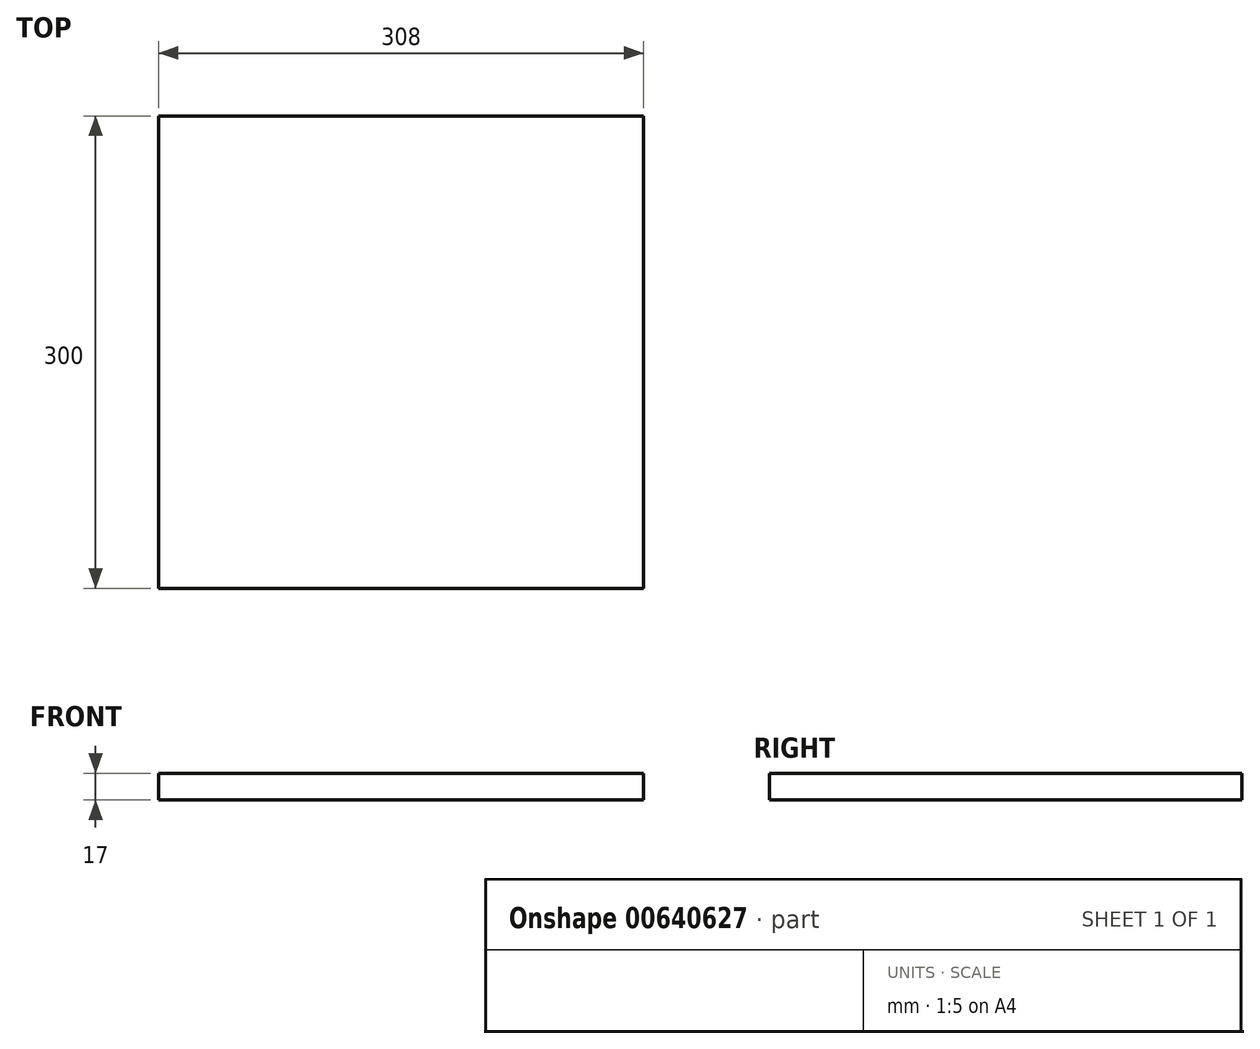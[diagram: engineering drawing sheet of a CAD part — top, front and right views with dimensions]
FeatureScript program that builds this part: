
annotation { "Feature Type Name" : "Feature", "Feature Type Description" : "" }
export const myFeature = defineFeature(function(context is Context, id is Id, definition is map)
    precondition{}
    {
        {
            var Q0;
            Q0=qCreatedBy(makeId("Top.planeOp"),FACE);
            var sketch = newSketch(context, id + "F0", { "sketchPlane" : qUnion([Q0])});
            skLineSegment(sketch, "E0.bottom", {"start": v(0, 0) * mm, "end": v(308, 0) * mm});
            skLineSegment(sketch, "E0.top", {"start": v(0, 300) * mm, "end": v(308, 300) * mm});
            skLineSegment(sketch, "E0.left", {"start": v(0, 0) * mm, "end": v(0, 300) * mm});
            skLineSegment(sketch, "E0.right", {"start": v(308, 0) * mm, "end": v(308, 300) * mm});
            skSolve(sketch);
        }
        {
            var Q0;
            Q0 = qSketchRegion(id + "F0", true);
            extrude(context, id + "F1", {"entities" : qUnion([Q0]), "depth" : 17 * mm, "offsetDistance" : 25 * mm});
        }
    });
